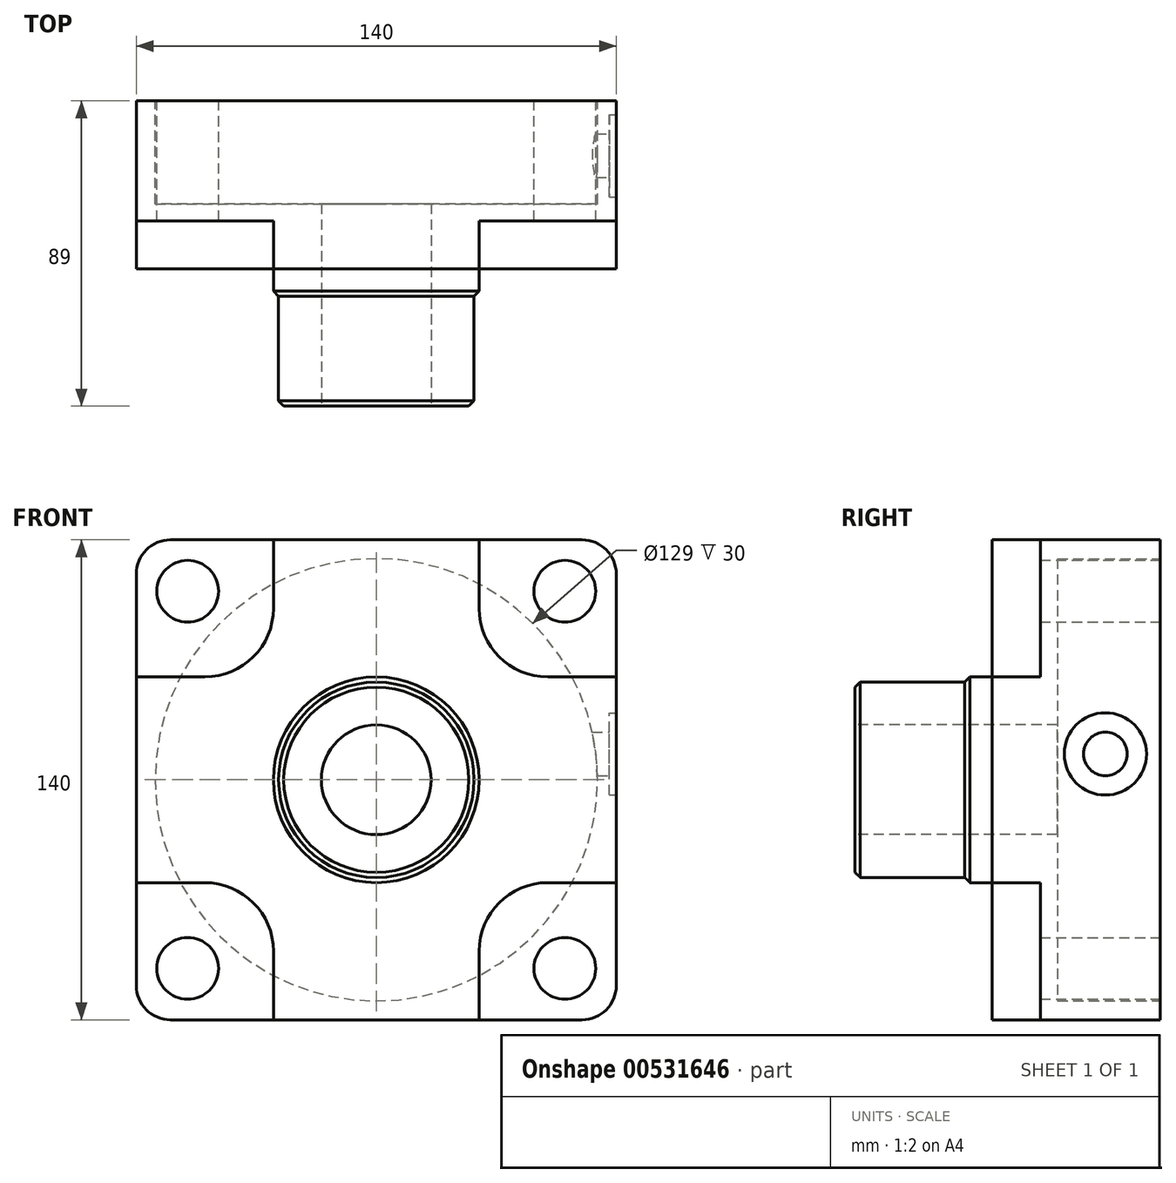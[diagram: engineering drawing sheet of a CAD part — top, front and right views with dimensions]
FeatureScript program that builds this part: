
annotation { "Feature Type Name" : "Feature", "Feature Type Description" : "" }
export const myFeature = defineFeature(function(context is Context, id is Id, definition is map)
    precondition{}
    {
        {
            var Q0;
            Q0=qCreatedBy(makeId("Front.planeOp"),FACE);
            var sketch = newSketch(context, id + "F0", { "sketchPlane" : qUnion([Q0])});
            skLineSegment(sketch, "E0.bottom", {"start": v(60, -70) * mm, "end": v(-60, -70) * mm});
            skLineSegment(sketch, "E0.top", {"start": v(60, 70) * mm, "end": v(-60, 70) * mm});
            skLineSegment(sketch, "E0.left", {"start": v(70, -60) * mm, "end": v(70, 60) * mm});
            skLineSegment(sketch, "E0.right", {"start": v(-70, -60) * mm, "end": v(-70, 60) * mm});
            skPoint(sketch, "E0.middle", {"position": v(0, 0) * mm});
            skPoint(sketch, "E1.visualSharp", {"position": v(-70, 70) * mm});
            skArc(sketch, "E1.filletArc", {"start": v(-60, 70) * mm, "mid": v(-67.07, 67.07) * mm, "end": v(-70, 60) * mm});
            skPoint(sketch, "E2.visualSharp", {"position": v(70, 70) * mm});
            skArc(sketch, "E2.filletArc", {"start": v(70, 60) * mm, "mid": v(67.07, 67.07) * mm, "end": v(60, 70) * mm});
            skPoint(sketch, "E3.visualSharp", {"position": v(70, -70) * mm});
            skArc(sketch, "E3.filletArc", {"start": v(60, -70) * mm, "mid": v(67.07, -67.07) * mm, "end": v(70, -60) * mm});
            skPoint(sketch, "E4.visualSharp", {"position": v(-70, -70) * mm});
            skArc(sketch, "E4.filletArc", {"start": v(-70, -60) * mm, "mid": v(-67.07, -67.07) * mm, "end": v(-60, -70) * mm});
            skLineSegment(sketch, "E5", {"start": v(0, 70) * mm, "end": v(0, -70) * mm, "construction": true});
            skLineSegment(sketch, "E6.0", {"start": v(-55, 47.5) * mm, "end": v(-55, -47.5) * mm, "construction": true});
            skLineSegment(sketch, "E7.0", {"start": v(55, 47.5) * mm, "end": v(55, -47.5) * mm, "construction": true});
            skLineSegment(sketch, "E8", {"start": v(-70, 0) * mm, "end": v(70, 0) * mm, "construction": true});
            skLineSegment(sketch, "E9.0", {"start": v(-47.5, -55) * mm, "end": v(47.5, -55) * mm, "construction": true});
            skLineSegment(sketch, "E10.0", {"start": v(-47.5, 55) * mm, "end": v(47.5, 55) * mm, "construction": true});
            skCircle(sketch, "E11", {"center": v(-55, 55) * mm, "radius": 9 * mm});
            skCircle(sketch, "E12", {"center": v(55, 55) * mm, "radius": 9 * mm});
            skCircle(sketch, "E13", {"center": v(-55, -55) * mm, "radius": 9 * mm});
            skCircle(sketch, "E14", {"center": v(55, -55) * mm, "radius": 9 * mm});
            skSolve(sketch);
        }
        {
            var Q0;
            Q0=makeQuery(id+"F0.imprint","IMPRINT",FACE,{"disambiguationData":[TD([[makeQuery(id+"F0.imprint","IMPRINT",EDGE,{"derivedFrom":sQuery(id+"F0.wireOp",EDGE,"E0.bottom")}),-1.0]])]});
            extrude(context, id + "F1", {"entities" : qUnion([Q0]), "endBound" : BoundingType.SYMMETRIC, "depth" : 49 * mm, "offsetDistance" : 25 * mm});
        }
        {
            var Q0;
            Q0=makeQuery(id+"F1.opExtrude","CAP_FACE",FACE,{"disambiguationData":[OSD([sQuery(id+"F0.wireOp",EDGE,"E0.bottom"),sQuery(id+"F0.wireOp",EDGE,"E0.top"),sQuery(id+"F0.wireOp",EDGE,"E0.left"),sQuery(id+"F0.wireOp",EDGE,"E0.right"),sQuery(id+"F0.wireOp",EDGE,"E1.filletArc"),sQuery(id+"F0.wireOp",EDGE,"E2.filletArc"),sQuery(id+"F0.wireOp",EDGE,"E3.filletArc"),sQuery(id+"F0.wireOp",EDGE,"E4.filletArc"),sQuery(id+"F0.wireOp",EDGE,"E11"),sQuery(id+"F0.wireOp",EDGE,"E12"),sQuery(id+"F0.wireOp",EDGE,"E13"),sQuery(id+"F0.wireOp",EDGE,"E14")])],"isStart":false});
            var sketch = newSketch(context, id + "F2", { "sketchPlane" : qUnion([Q0])});
            skLineSegment(sketch, "E15", {"start": v(-70, 30) * mm, "end": v(-50, 30) * mm});
            skLineSegment(sketch, "E16", {"start": v(-70, -30) * mm, "end": v(-50, -30) * mm});
            skLineSegment(sketch, "E17", {"start": v(-30, 70) * mm, "end": v(-30, 50) * mm});
            skLineSegment(sketch, "E18", {"start": v(30, 70) * mm, "end": v(30, 50) * mm});
            skLineSegment(sketch, "E19", {"start": v(50, 30) * mm, "end": v(70, 30) * mm});
            skLineSegment(sketch, "E20", {"start": v(50, -30) * mm, "end": v(70, -30) * mm});
            skLineSegment(sketch, "E21", {"start": v(30, -50) * mm, "end": v(30, -70) * mm});
            skLineSegment(sketch, "E22", {"start": v(-30, -50) * mm, "end": v(-30, -70) * mm});
            skArc(sketch, "E23.filletArc", {"start": v(-50, 30) * mm, "mid": v(-35.86, 35.86) * mm, "end": v(-30, 50) * mm});
            skPoint(sketch, "E24.newPointA", {"position": v(0.48, 30) * mm});
            skArc(sketch, "E24.filletArc", {"start": v(30, 50) * mm, "mid": v(35.86, 35.86) * mm, "end": v(50, 30) * mm});
            skPoint(sketch, "E25.newPointB", {"position": v(-30, -0.08) * mm});
            skArc(sketch, "E25.filletArc", {"start": v(-30, -50) * mm, "mid": v(-35.86, -35.86) * mm, "end": v(-50, -30) * mm});
            skPoint(sketch, "E26.newPointA", {"position": v(1.13, -30) * mm});
            skPoint(sketch, "E26.newPointB", {"position": v(30, -0.08) * mm});
            skArc(sketch, "E26.filletArc", {"start": v(50, -30) * mm, "mid": v(35.86, -35.86) * mm, "end": v(30, -50) * mm});
            skLineSegment(sketch, "E27.0", {"start": v(-70, -60) * mm, "end": v(-70, -30) * mm});
            skArc(sketch, "E28.0", {"start": v(-60, 70) * mm, "mid": v(-67.07, 67.07) * mm, "end": v(-70, 60) * mm});
            skLineSegment(sketch, "E29.0", {"start": v(60, 70) * mm, "end": v(30, 70) * mm});
            skPoint(sketch, "E30.0", {"position": v(67.07, 67.07) * mm});
            skArc(sketch, "E31.0", {"start": v(70, 60) * mm, "mid": v(67.07, 67.07) * mm, "end": v(60, 70) * mm});
            skLineSegment(sketch, "E32.0", {"start": v(70, -60) * mm, "end": v(70, -30) * mm});
            skPoint(sketch, "E33.0", {"position": v(67.07, -67.07) * mm});
            skArc(sketch, "E34.0", {"start": v(60, -70) * mm, "mid": v(67.07, -67.07) * mm, "end": v(70, -60) * mm});
            skLineSegment(sketch, "E35.0", {"start": v(60, -70) * mm, "end": v(30, -70) * mm});
            skArc(sketch, "E36.0", {"start": v(-70, -60) * mm, "mid": v(-67.07, -67.07) * mm, "end": v(-60, -70) * mm});
            skPoint(sketch, "E37.orphan", {"position": v(-51.1, 30) * mm});
            skPoint(sketch, "E38.orphan", {"position": v(-30, 52.95) * mm});
            skLineSegment(sketch, "E39.trimOffspring", {"start": v(-30, 70) * mm, "end": v(-60, 70) * mm});
            skLineSegment(sketch, "E40.trimOffspring", {"start": v(-70, 30) * mm, "end": v(-70, 60) * mm});
            skPoint(sketch, "E41.orphan", {"position": v(-30, -53.12) * mm});
            skPoint(sketch, "E42.orphan", {"position": v(-51.1, -30) * mm});
            skLineSegment(sketch, "E43.trimOffspring", {"start": v(-30, -70) * mm, "end": v(-60, -70) * mm});
            skPoint(sketch, "E44.orphan", {"position": v(30, -51.66) * mm});
            skPoint(sketch, "E45.orphan", {"position": v(53.36, -30) * mm});
            skPoint(sketch, "E46.orphan", {"position": v(52.07, 30) * mm});
            skPoint(sketch, "E47.orphan", {"position": v(30, 51.5) * mm});
            skLineSegment(sketch, "E48.trimOffspring", {"start": v(70, 30) * mm, "end": v(70, 60) * mm});
            skSolve(sketch);
        }
        {
            var Q0;
            Q0=makeQuery(id+"F2.imprint","IMPRINT",FACE,{"disambiguationData":[TD([[makeQuery(id+"F2.imprint","IMPRINT",EDGE,{"derivedFrom":sQuery(id+"F2.wireOp",EDGE,"E20")}),-1.0]])]});
            var Q1;
            Q1=makeQuery(id+"F2.imprint","IMPRINT",FACE,{"disambiguationData":[TD([[makeQuery(id+"F2.imprint","IMPRINT",EDGE,{"derivedFrom":sQuery(id+"F2.wireOp",EDGE,"E18")}),1.0]])]});
            var Q2;
            Q2=makeQuery(id+"F2.imprint","IMPRINT",FACE,{"disambiguationData":[TD([[makeQuery(id+"F2.imprint","IMPRINT",EDGE,{"derivedFrom":sQuery(id+"F2.wireOp",EDGE,"E15")}),1.0]])]});
            var Q3;
            Q3=makeQuery(id+"F2.imprint","IMPRINT",FACE,{"disambiguationData":[TD([[makeQuery(id+"F2.imprint","IMPRINT",EDGE,{"derivedFrom":sQuery(id+"F2.wireOp",EDGE,"E16")}),-1.0]])]});
            extrude(context, id + "F3", {"entities" : qUnion([Q0, Q1, Q2, Q3]), "operationType" : NewBodyOperationType.REMOVE, "oppositeDirection" : true, "depth" : 14 * mm, "offsetDistance" : 25 * mm});
        }
        {
            var Q0;
            Q0=makeQuery(id+"F1.opExtrude","CAP_FACE",FACE,{"disambiguationData":[OSD([sQuery(id+"F0.wireOp",EDGE,"E0.bottom"),sQuery(id+"F0.wireOp",EDGE,"E0.top"),sQuery(id+"F0.wireOp",EDGE,"E0.left"),sQuery(id+"F0.wireOp",EDGE,"E0.right"),sQuery(id+"F0.wireOp",EDGE,"E1.filletArc"),sQuery(id+"F0.wireOp",EDGE,"E2.filletArc"),sQuery(id+"F0.wireOp",EDGE,"E3.filletArc"),sQuery(id+"F0.wireOp",EDGE,"E4.filletArc"),sQuery(id+"F0.wireOp",EDGE,"E11"),sQuery(id+"F0.wireOp",EDGE,"E12"),sQuery(id+"F0.wireOp",EDGE,"E13"),sQuery(id+"F0.wireOp",EDGE,"E14")])],"isStart":false});
            var sketch = newSketch(context, id + "F4", { "sketchPlane" : qUnion([Q0])});
            skCircle(sketch, "E49", {"center": v(0, 0) * mm, "radius": 30 * mm});
            skSolve(sketch);
        }
        {
            var Q0;
            Q0=makeQuery(id+"F4.imprint","IMPRINT",FACE,{"disambiguationData":[TD([[makeQuery(id+"F4.imprint","IMPRINT",EDGE,{"derivedFrom":sQuery(id+"F4.wireOp",EDGE,"E49")}),1.0]])]});
            extrude(context, id + "F5", {"entities" : qUnion([Q0]), "operationType" : NewBodyOperationType.ADD, "depth" : 8 * mm, "offsetDistance" : 25 * mm});
        }
        {
            var Q0;
            Q0=makeQuery(id+"F5.opExtrude","CAP_EDGE",EDGE,{"disambiguationData":[OSD([sQuery(id+"F4.wireOp",EDGE,"E49")])],"isStart":false});
            chamfer(context, id + "F6", {"entities" : qUnion([Q0]), "width" : 1.5 * mm, "tangentPropagation" : true});
        }
        {
            var Q0;
            Q0=makeQuery(id+"F5.opExtrude","CAP_FACE",FACE,{"disambiguationData":[OSD([sQuery(id+"F4.wireOp",EDGE,"E49")])],"isStart":false});
            var sketch = newSketch(context, id + "F7", { "sketchPlane" : qUnion([Q0])});
            skCircle(sketch, "E50.0", {"center": v(0, 0) * mm, "radius": 28.5 * mm});
            skSolve(sketch);
        }
        {
            var Q0;
            Q0=makeQuery(id+"F7.imprint","IMPRINT",FACE,{"disambiguationData":[TD([[makeQuery(id+"F7.imprint","IMPRINT",EDGE,{"derivedFrom":sQuery(id+"F7.wireOp",EDGE,"E50.0")}),1.0]])]});
            extrude(context, id + "F8", {"entities" : qUnion([Q0]), "operationType" : NewBodyOperationType.ADD, "depth" : 32 * mm, "offsetDistance" : 25 * mm});
        }
        {
            var Q0;
            Q0=makeQuery(id+"F8.opExtrude","CAP_EDGE",EDGE,{"disambiguationData":[OSD([sQuery(id+"F7.wireOp",EDGE,"E50.0")])],"isStart":false});
            chamfer(context, id + "F9", {"entities" : qUnion([Q0]), "width" : 1.5 * mm, "tangentPropagation" : true});
        }
        {
            var Q0;
            Q0=makeQuery(id+"F8.opExtrude","CAP_FACE",FACE,{"disambiguationData":[OSD([sQuery(id+"F7.wireOp",EDGE,"E50.0")])],"isStart":false});
            var sketch = newSketch(context, id + "F10", { "sketchPlane" : qUnion([Q0])});
            skCircle(sketch, "E51", {"center": v(0, 0) * mm, "radius": 16 * mm});
            skSolve(sketch);
        }
        {
            var Q0;
            Q0=makeQuery(id+"F10.imprint","IMPRINT",FACE,{"disambiguationData":[TD([[makeQuery(id+"F10.imprint","IMPRINT",EDGE,{"derivedFrom":sQuery(id+"F10.wireOp",EDGE,"E51")}),1.0]])]});
            extrude(context, id + "F11", {"entities" : qUnion([Q0]), "operationType" : NewBodyOperationType.REMOVE, "endBound" : BoundingType.THROUGH_ALL, "oppositeDirection" : true, "depth" : 25 * mm});
        }
        {
            var Q0;
            Q0=makeQuery(id+"F1.opExtrude","CAP_FACE",FACE,{"disambiguationData":[OSD([sQuery(id+"F0.wireOp",EDGE,"E0.bottom"),sQuery(id+"F0.wireOp",EDGE,"E0.top"),sQuery(id+"F0.wireOp",EDGE,"E0.left"),sQuery(id+"F0.wireOp",EDGE,"E0.right"),sQuery(id+"F0.wireOp",EDGE,"E1.filletArc"),sQuery(id+"F0.wireOp",EDGE,"E2.filletArc"),sQuery(id+"F0.wireOp",EDGE,"E3.filletArc"),sQuery(id+"F0.wireOp",EDGE,"E4.filletArc"),sQuery(id+"F0.wireOp",EDGE,"E11"),sQuery(id+"F0.wireOp",EDGE,"E12"),sQuery(id+"F0.wireOp",EDGE,"E13"),sQuery(id+"F0.wireOp",EDGE,"E14")])],"isStart":true});
            var sketch = newSketch(context, id + "F12", { "sketchPlane" : qUnion([Q0])});
            skCircle(sketch, "E52", {"center": v(0, 0) * mm, "radius": 64.5 * mm});
            skSolve(sketch);
        }
        {
            var Q0;
            Q0=makeQuery(id+"F12.imprint","IMPRINT",FACE,{"disambiguationData":[TD([[makeQuery(id+"F12.imprint","IMPRINT",EDGE,{"derivedFrom":sQuery(id+"F12.wireOp",EDGE,"E52")}),1.0]])]});
            extrude(context, id + "F13", {"entities" : qUnion([Q0]), "operationType" : NewBodyOperationType.REMOVE, "oppositeDirection" : true, "depth" : 30 * mm, "offsetDistance" : 25 * mm});
        }
        {
            var Q0;
            Q0=makeQuery(id+"F1.opExtrude","SWEPT_FACE",FACE,{"disambiguationData":[OSD([sQuery(id+"F0.wireOp",EDGE,"E0.left")])]});
            var sketch = newSketch(context, id + "F14", { "sketchPlane" : qUnion([Q0])});
            skLineSegment(sketch, "E53", {"start": v(8.5, 48.9) * mm, "end": v(8.5, -49.62) * mm, "construction": true});
            skCircle(sketch, "E54", {"center": v(8.5, 7.55) * mm, "radius": 6.35 * mm});
            skCircle(sketch, "E55", {"center": v(8.5, 7.55) * mm, "radius": 12 * mm});
            skSolve(sketch);
        }
        {
            var Q0;
            Q0=makeQuery(id+"F14.imprint","IMPRINT",FACE,{"disambiguationData":[TD([[makeQuery(id+"F14.imprint","IMPRINT",EDGE,{"derivedFrom":sQuery(id+"F14.wireOp",EDGE,"E54")}),-1.0]])]});
            extrude(context, id + "F15", {"entities" : qUnion([Q0]), "operationType" : NewBodyOperationType.REMOVE, "oppositeDirection" : true, "depth" : 2 * mm});
        }
        {
            var Q0;
            Q0=makeQuery(id+"F15.boolean.opBoolean","SPLIT",FACE,{"disambiguationData":[TD([makeQuery(id+"F15.opExtrude","SWEPT_FACE",FACE,{"disambiguationData":[OSD([sQuery(id+"F14.wireOp",EDGE,"E54")])]})])],"derivedFrom":makeQuery(id+"F1.opExtrude","SWEPT_FACE",FACE,{"disambiguationData":[OSD([sQuery(id+"F0.wireOp",EDGE,"E0.left")])]})});
            extrude(context, id + "F16", {"entities" : qUnion([Q0]), "operationType" : NewBodyOperationType.REMOVE, "oppositeDirection" : true, "depth" : 9 * mm});
        }
    });
